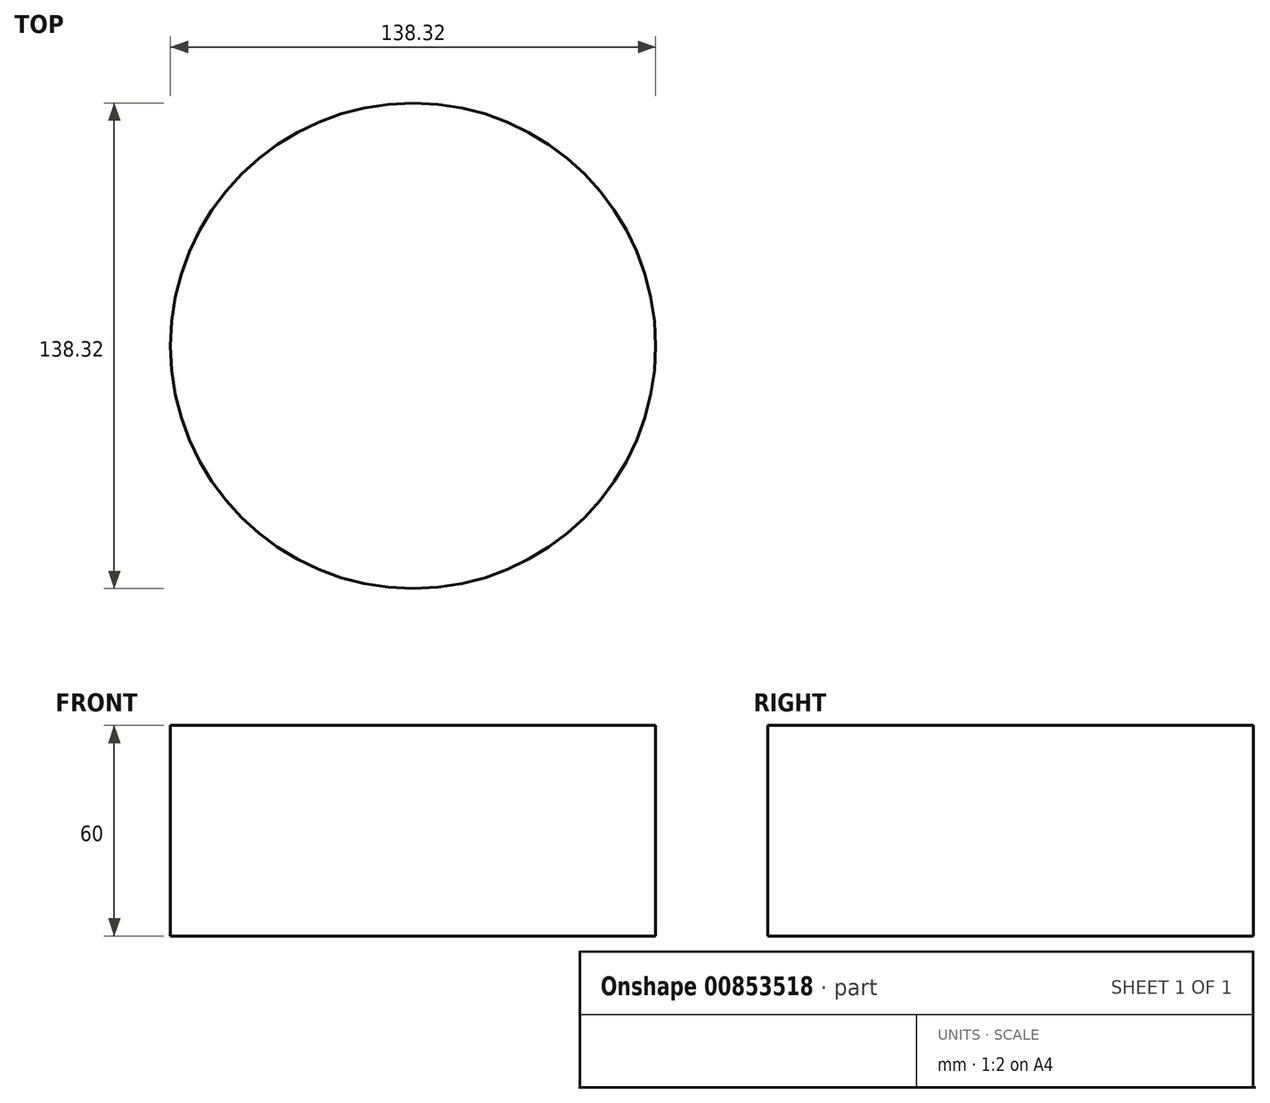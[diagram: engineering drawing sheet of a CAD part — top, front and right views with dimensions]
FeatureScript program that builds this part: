
annotation { "Feature Type Name" : "Feature", "Feature Type Description" : "" }
export const myFeature = defineFeature(function(context is Context, id is Id, definition is map)
    precondition{}
    {
        {
            var Q0;
            Q0=qCreatedBy(makeId("Top.planeOp"),FACE);
            var sketch = newSketch(context, id + "F0", { "sketchPlane" : qUnion([Q0])});
            skCircle(sketch, "E0", {"center": v(0, 0) * mm, "radius": 69.16 * mm});
            skSolve(sketch);
        }
        {
            var Q0;
            Q0 = qSketchRegion(id + "F0", true);
            var sketch = newSketch(context, id + "F1", { "sketchPlane" : qUnion([Q0])});
            skSolve(sketch);
        }
        {
            var Q0;
            Q0=makeQuery(id+"F1.imprint","IMPRINT",FACE,{"disambiguationData":[TD([[makeQuery(id+"F1.imprint","IMPRINT",EDGE,{"derivedFrom":makeQuery(id+"F0.imprint","IMPRINT",EDGE,{"derivedFrom":sQuery(id+"F0.wireOp",EDGE,"E0")})}),1.0]])]});
            extrude(context, id + "F2", {"entities" : qUnion([Q0]), "depth" : 60 * mm, "offsetDistance" : 25 * mm});
        }
        {
            var Q0;
            Q0=makeQuery(id+"F0.imprint","IMPRINT",FACE,{"disambiguationData":[TD([[makeQuery(id+"F0.imprint","IMPRINT",EDGE,{"derivedFrom":sQuery(id+"F0.wireOp",EDGE,"E0")}),1.0]])]});
            var sketch = newSketch(context, id + "F3", { "sketchPlane" : qUnion([Q0])});
            skCircle(sketch, "E1", {"center": v(0, 0) * mm, "radius": 35.71 * mm});
            skSolve(sketch);
        }
        {
            var Q0;
            Q0=makeQuery(id+"F3.imprint","IMPRINT",FACE,{"disambiguationData":[TD([[makeQuery(id+"F3.imprint","IMPRINT",EDGE,{"derivedFrom":sQuery(id+"F3.wireOp",EDGE,"E1")}),-1.0]])]});
            extrude(context, id + "F4", {"entities" : qUnion([Q0]), "operationType" : NewBodyOperationType.ADD, "depth" : 25 * mm, "offsetDistance" : 25 * mm});
        }
        {
            var Q0;
            Q0=sQuery(id+"F3.wireOp",EDGE,"E1");
            extrude(context, id + "F5", {"bodyType" : ToolBodyType.SURFACE, "surfaceEntities" : qUnion([Q0]), "oppositeDirection" : true, "depth" : 150 * mm, "offsetDistance" : 25 * mm});
        }
    });
